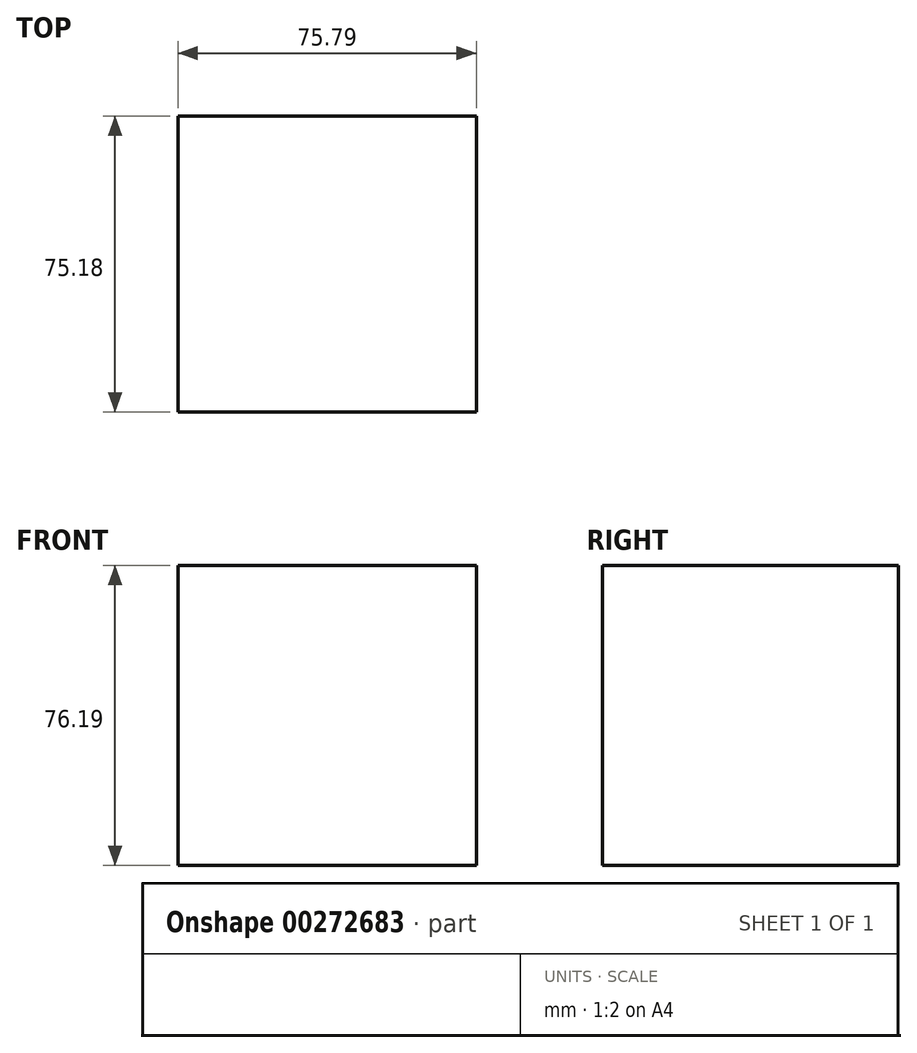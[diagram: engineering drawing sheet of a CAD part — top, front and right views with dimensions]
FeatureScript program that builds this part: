
annotation { "Feature Type Name" : "Feature", "Feature Type Description" : "" }
export const myFeature = defineFeature(function(context is Context, id is Id, definition is map)
    precondition{}
    {
        {
            var Q0;
            Q0=qCreatedBy(makeId("Front.planeOp"),FACE);
            var sketch = newSketch(context, id + "F0", { "sketchPlane" : qUnion([Q0])});
            skLineSegment(sketch, "E0", {"start": v(0, 0) * mm, "end": v(-75.8, 0) * mm});
            skLineSegment(sketch, "E1", {"start": v(-75.8, 0) * mm, "end": v(-75.8, 76.2) * mm});
            skLineSegment(sketch, "E2", {"start": v(-75.8, 76.2) * mm, "end": v(0, 76.2) * mm});
            skLineSegment(sketch, "E3", {"start": v(0, 76.2) * mm, "end": v(0, 0) * mm});
            skLineSegment(sketch, "E4", {"start": v(0, 0) * mm, "end": v(-37.9, 0) * mm});
            skLineSegment(sketch, "E5", {"start": v(-37.9, 0) * mm, "end": v(-37.9, 35.33) * mm});
            skLineSegment(sketch, "E6", {"start": v(-37.9, 35.33) * mm, "end": v(0, 35.33) * mm});
            skSolve(sketch);
        }
        {
            var Q0;
            Q0 = qSketchRegion(id + "F0", true);
            extrude(context, id + "F1", {"entities" : qUnion([Q0]), "depth" : 75.18 * mm});
        }
    });
